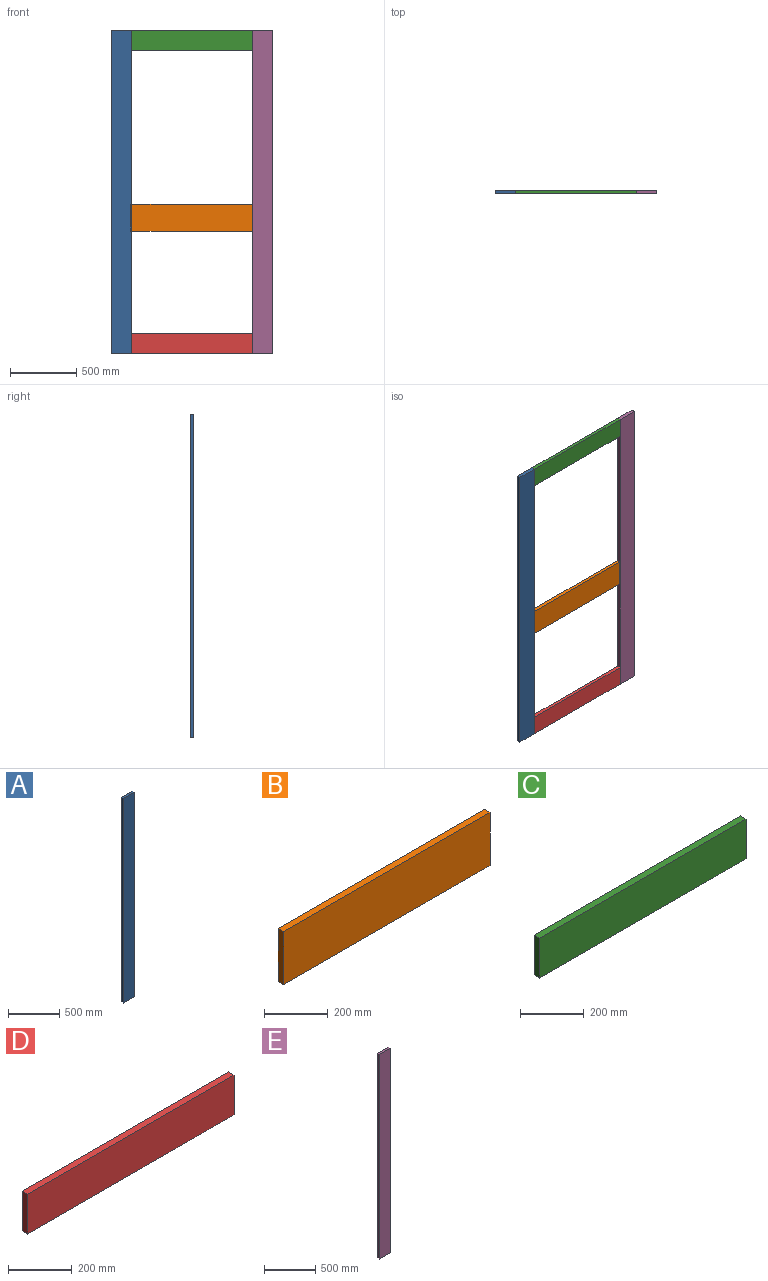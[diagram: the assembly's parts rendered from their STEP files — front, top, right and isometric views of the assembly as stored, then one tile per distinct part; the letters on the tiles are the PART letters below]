
ASSEMBLY  parts=5 mates=5
PART A: 6 faces, bbox 152.4x25.4x2438.4 mm
  f0: plane 2438.4x25.4mm, normal (-1,0,0), area 61935.4mm2, adj f1,f3,f4,f5
  f1: plane 152.4x25.4mm, normal (0,0,-1), area 3871mm2, adj f0,f2,f4,f5
  f2: plane 2438.4x25.4mm, normal (1,0,0), area 61935.4mm2, adj f1,f3,f4,f5
  f3: plane 152.4x25.4mm, normal (0,0,1), area 3871mm2, adj f0,f2,f4,f5
  f4: plane 2438.4x152.4mm, normal (0,-1,0), area 371612.2mm2, adj f0,f1,f2,f3
  f5: plane 2438.4x152.4mm, normal (0,1,0), area 371612.2mm2, adj f0,f1,f2,f3
PART B: 6 faces, bbox 914.4x25.4x203.2 mm
  f0: plane 203.2x25.4mm, normal (-1,0,0), area 5161.3mm2, adj f1,f3,f4,f5
  f1: plane 914.4x25.4mm, normal (0,0,-1), area 23225.8mm2, adj f0,f2,f4,f5
  f2: plane 203.2x25.4mm, normal (1,0,0), area 5161.3mm2, adj f1,f3,f4,f5
  f3: plane 914.4x25.4mm, normal (0,0,1), area 23225.8mm2, adj f0,f2,f4,f5
  f4: plane 914.4x203.2mm, normal (0,-1,0), area 185806.1mm2, adj f0,f1,f2,f3
  f5: plane 914.4x203.2mm, normal (0,1,0), area 185806.1mm2, adj f0,f1,f2,f3
PART C: 6 faces, bbox 914.4x25.4x152.4 mm
  f0: plane 152.4x25.4mm, normal (-1,0,0), area 3871mm2, adj f1,f3,f4,f5
  f1: plane 914.4x25.4mm, normal (0,0,-1), area 23225.8mm2, adj f0,f2,f4,f5
  f2: plane 152.4x25.4mm, normal (1,0,0), area 3871mm2, adj f1,f3,f4,f5
  f3: plane 914.4x25.4mm, normal (0,0,1), area 23225.8mm2, adj f0,f2,f4,f5
  f4: plane 914.4x152.4mm, normal (0,-1,0), area 139354.6mm2, adj f0,f1,f2,f3
  f5: plane 914.4x152.4mm, normal (0,1,0), area 139354.6mm2, adj f0,f1,f2,f3
PART D: 6 faces, bbox 914.4x25.4x152.4 mm
  f0: plane 152.4x25.4mm, normal (-1,0,0), area 3871mm2, adj f1,f3,f4,f5
  f1: plane 914.4x25.4mm, normal (0,0,-1), area 23225.8mm2, adj f0,f2,f4,f5
  f2: plane 152.4x25.4mm, normal (1,0,0), area 3871mm2, adj f1,f3,f4,f5
  f3: plane 914.4x25.4mm, normal (0,0,1), area 23225.8mm2, adj f0,f2,f4,f5
  f4: plane 914.4x152.4mm, normal (0,-1,0), area 139354.6mm2, adj f0,f1,f2,f3
  f5: plane 914.4x152.4mm, normal (0,1,0), area 139354.6mm2, adj f0,f1,f2,f3
PART E: 6 faces, bbox 152.4x25.4x2438.4 mm
  f0: plane 2438.4x25.4mm, normal (-1,0,0), area 61935.4mm2, adj f1,f3,f4,f5
  f1: plane 152.4x25.4mm, normal (0,0,-1), area 3871mm2, adj f0,f2,f4,f5
  f2: plane 2438.4x25.4mm, normal (1,0,0), area 61935.4mm2, adj f1,f3,f4,f5
  f3: plane 152.4x25.4mm, normal (0,0,1), area 3871mm2, adj f0,f2,f4,f5
  f4: plane 2438.4x152.4mm, normal (0,-1,0), area 371612.2mm2, adj f0,f1,f2,f3
  f5: plane 2438.4x152.4mm, normal (0,1,0), area 371612.2mm2, adj f0,f1,f2,f3
PLACE A t=(165.94,-9.89,-16.7)mm fixed
PLACE B t=(-147.29,-9.89,144.08)mm
PLACE C t=(5.32,-9.89,82.19)mm fixed
PLACE D t=(19.48,-9.89,-36.36)mm
PLACE E t=(-249.98,-9.89,-12.2)mm
MATE parallel C.f2 <-> E.f0  axis (1,0,0) through (940.94,-22.59,1273.22)mm
MATE parallel E.f0 <-> C.f2  axis (-1,0,0) through (940.94,-22.59,1273.22)mm
MATE parallel A.f2 <-> D.f0  axis (1,0,0) through (26.54,-22.59,-1165.18)mm
MATE parallel C.f0 <-> A.f2  axis (-1,0,0) through (26.54,-22.59,1273.22)mm
MATE parallel A.f2 <-> B.f0  axis (1,0,0) through (26.54,-22.59,54.02)mm
